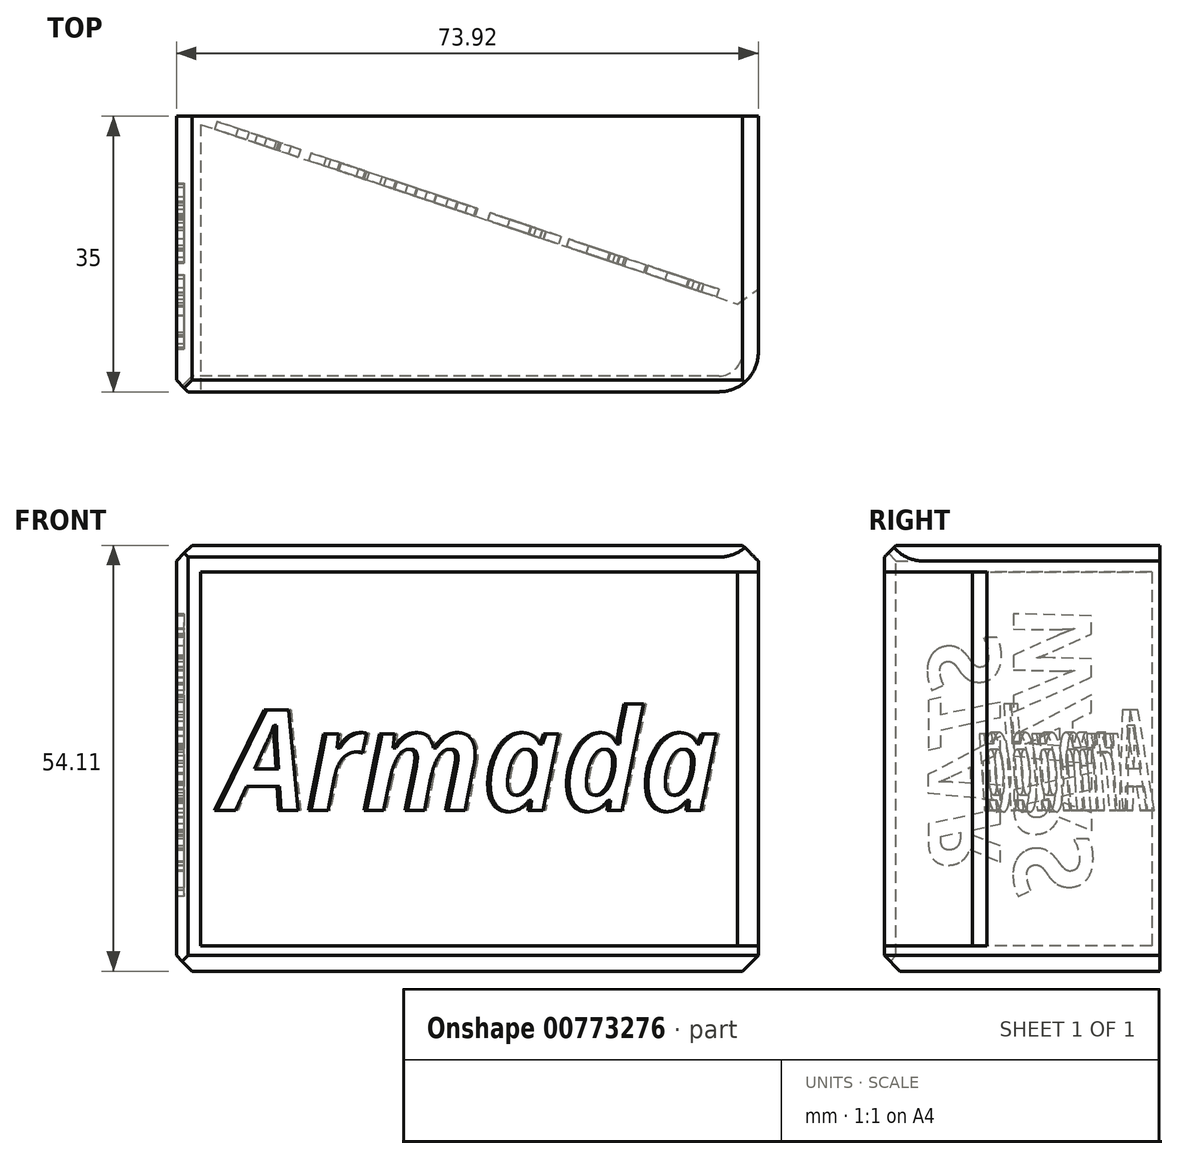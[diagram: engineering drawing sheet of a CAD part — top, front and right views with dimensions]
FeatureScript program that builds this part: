
annotation { "Feature Type Name" : "Feature", "Feature Type Description" : "" }
export const myFeature = defineFeature(function(context is Context, id is Id, definition is map)
    precondition{}
    {
        {
            var Q0;
            Q0=qCreatedBy(makeId("Front.planeOp"),FACE);
            var sketch = newSketch(context, id + "F0", { "sketchPlane" : qUnion([Q0])});
            skLineSegment(sketch, "E0", {"start": v(31.06, 0) * mm, "end": v(-42.86, 0) * mm});
            skLineSegment(sketch, "E1", {"start": v(-42.86, 0) * mm, "end": v(-42.86, 54.1) * mm});
            skLineSegment(sketch, "E2", {"start": v(-42.86, 54.1) * mm, "end": v(31.06, 54.1) * mm});
            skLineSegment(sketch, "E3", {"start": v(31.06, 54.1) * mm, "end": v(31.06, 50.73) * mm});
            skLineSegment(sketch, "E4", {"start": v(31.06, 50.73) * mm, "end": v(-39.77, 50.73) * mm});
            skLineSegment(sketch, "E5", {"start": v(-39.77, 50.73) * mm, "end": v(-39.77, 3.23) * mm});
            skLineSegment(sketch, "E6", {"start": v(-39.77, 3.23) * mm, "end": v(31.06, 3.23) * mm});
            skLineSegment(sketch, "E7", {"start": v(31.06, 3.23) * mm, "end": v(31.06, 0) * mm});
            skSolve(sketch);
        }
        {
            var Q0;
            Q0=qSketchRegion(id+"F0",true);
            extrude(context, id + "F1", {"entities" : qUnion([Q0]), "oppositeDirection" : true, "depth" : 35 * mm, "offsetDistance" : 25 * mm});
        }
        {
            var Q0;
            Q0=makeQuery(id+"F1.opExtrude","SWEPT_FACE",FACE,{"disambiguationData":[OSD([sQuery(id+"F0.wireOp",EDGE,"E0")])]});
            var sketch = newSketch(context, id + "F2", { "sketchPlane" : qUnion([Q0])});
            skLineSegment(sketch, "E8", {"start": v(-42.86, -35) * mm, "end": v(31.06, -10.29) * mm});
            skLineSegment(sketch, "E9", {"start": v(31.06, -10.29) * mm, "end": v(31.06, -35) * mm});
            skLineSegment(sketch, "E10", {"start": v(31.06, -35) * mm, "end": v(-42.86, -35) * mm});
            skSolve(sketch);
        }
        {
            var Q0;
            Q0=makeQuery(id+"F2.imprint","IMPRINT",FACE,{"disambiguationData":[TD([[makeQuery(id+"F2.imprint","IMPRINT",EDGE,{"derivedFrom":sQuery(id+"F2.wireOp",EDGE,"E8")}),-1.0]])]});
            extrude(context, id + "F3", {"entities" : qUnion([Q0]), "operationType" : NewBodyOperationType.ADD, "oppositeDirection" : true, "depth" : 54 * mm, "offsetDistance" : 25 * mm});
        }
        {
            var Q0;
            Q0=makeQuery(id+"F1.opExtrude","CAP_EDGE",EDGE,{"disambiguationData":[OSD([sQuery(id+"F0.wireOp",EDGE,"E0")])],"isStart":true});
            var Q1;
            Q1=makeQuery(id+"F1.opExtrude","CAP_EDGE",EDGE,{"disambiguationData":[OSD([sQuery(id+"F0.wireOp",EDGE,"E1")])],"isStart":true});
            var Q2;
            Q2=makeQuery(id+"F1.opExtrude","CAP_EDGE",EDGE,{"disambiguationData":[OSD([sQuery(id+"F0.wireOp",EDGE,"E2")])],"isStart":true});
            chamfer(context, id + "F4", {"entities" : qUnion([Q0, Q1, Q2]), "width" : 1.5 * mm, "tangentPropagation" : true});
        }
        {
            var Q0;
            Q0=makeQuery(id+"F1.opExtrude","CAP_EDGE",EDGE,{"disambiguationData":[OSD([sQuery(id+"F0.wireOp",EDGE,"E3")])],"isStart":true});
            var Q1;
            Q1=makeQuery(id+"F1.opExtrude","CAP_EDGE",EDGE,{"disambiguationData":[OSD([sQuery(id+"F0.wireOp",EDGE,"E7")])],"isStart":true});
            fillet(context, id + "F5", {"entities" : qUnion([Q0, Q1]), "radius" : 5 * mm, "tangentPropagation" : true, "allowEdgeOverflow" : false});
        }
        {
            var Q0;
            Q0=makeQuery(id+"F3.opExtrude","SWEPT_EDGE",EDGE,{"disambiguationData":[OSD([sQuery(id+"F0.wireOp",EDGE,"E0"),sQuery(id+"F0.wireOp",EDGE,"E7"),sQuery(id+"F2.wireOp",EDGE,"E8"),sQuery(id+"F2.wireOp",EDGE,"E9")])]});
            chamfer(context, id + "F6", {"entities" : qUnion([Q0]), "width" : 2 * mm, "tangentPropagation" : true});
        }
        {
            var Q0;
            Q0=makeQuery(id+"F1.opExtrude","SWEPT_EDGE",EDGE,{"disambiguationData":[OSD([sQuery(id+"F0.wireOp",EDGE,"E0"),sQuery(id+"F0.wireOp",EDGE,"E1")])]});
            var Q1;
            Q1=makeQuery(id+"F1.opExtrude","SWEPT_EDGE",EDGE,{"disambiguationData":[OSD([sQuery(id+"F0.wireOp",EDGE,"E1"),sQuery(id+"F0.wireOp",EDGE,"E2")])]});
            chamfer(context, id + "F7", {"entities" : qUnion([Q0, Q1]), "width" : 2 * mm, "tangentPropagation" : true});
        }
        {
            var Q0;
            Q0=makeQuery(id+"F1.opExtrude","SWEPT_EDGE",EDGE,{"disambiguationData":[OSD([sQuery(id+"F0.wireOp",EDGE,"E2"),sQuery(id+"F0.wireOp",EDGE,"E3")])]});
            var Q1;
            Q1=makeQuery(id+"F1.opExtrude","SWEPT_EDGE",EDGE,{"disambiguationData":[OSD([sQuery(id+"F0.wireOp",EDGE,"E0"),sQuery(id+"F0.wireOp",EDGE,"E7")])]});
            chamfer(context, id + "F8", {"entities" : qUnion([Q0, Q1]), "width" : 2 * mm, "tangentPropagation" : true});
        }
        {
            var Q0;
            Q0=makeQuery(id+"F3.opExtrude","SWEPT_FACE",FACE,{"disambiguationData":[OSD([sQuery(id+"F2.wireOp",EDGE,"E8")])]});
            var sketch = newSketch(context, id + "F9", { "sketchPlane" : qUnion([Q0])});
            skText(sketch, "E11", { "text": "Armada", "fontName": "OpenSans-BoldItalic.ttf"});
            const initialGuessF9  = {"E11": [-0.04556, 0.02043, 1, 0, 0.0128]};
            skSetInitialGuess(sketch, initialGuessF9);
            skSolve(sketch);
        }
        {
            var Q0;
            Q0 = qSketchRegion(id + "F9", true);
            extrude(context, id + "F10", {"entities" : qUnion([Q0]), "operationType" : NewBodyOperationType.REMOVE, "oppositeDirection" : true, "depth" : 1 * mm, "offsetDistance" : 25 * mm});
        }
        {
            var Q0;
            Q0=makeQuery(id+"F1.opExtrude","SWEPT_FACE",FACE,{"disambiguationData":[OSD([sQuery(id+"F0.wireOp",EDGE,"E1")])]});
            var sketch = newSketch(context, id + "F11", { "sketchPlane" : qUnion([Q0])});
            skText(sketch, "E12", { "text": "STAR", "fontName": "OpenSans-BoldItalic.ttf"});
            const initialGuessF11  = {"E12": [-0.01474, 0.04264, -0.00095, -1, 0.00924]};
            skSetInitialGuess(sketch, initialGuessF11);
            skSolve(sketch);
        }
        {
            var Q0;
            Q0=makeQuery(id+"F11.imprint","IMPRINT",FACE,{"disambiguationData":[TD([[makeQuery(id+"F11.imprint","IMPRINT",EDGE,{"derivedFrom":sQuery(id+"F11.wireOp",EDGE,"E12.sketch_text.stroke-0")}),1.0]])]});
            var sketch = newSketch(context, id + "F12", { "sketchPlane" : qUnion([Q0])});
            skText(sketch, "E13", { "text": "WARS", "fontName": "OpenSans-BoldItalic.ttf"});
            const initialGuessF12  = {"E13": [-0.02629, 0.04668, -0.00337, -1, 0.01]};
            skSetInitialGuess(sketch, initialGuessF12);
            skSolve(sketch);
        }
        {
            var Q0;
            Q0 = qSketchRegion(id + "F11", true);
            var Q1;
            Q1 = qSketchRegion(id + "F12", true);
            extrude(context, id + "F13", {"entities" : qUnion([Q0, Q1]), "operationType" : NewBodyOperationType.REMOVE, "oppositeDirection" : true, "depth" : 1 * mm, "offsetDistance" : 25 * mm});
        }
    });
